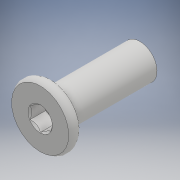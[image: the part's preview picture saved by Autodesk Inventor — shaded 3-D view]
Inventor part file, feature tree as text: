
AUTODESK INVENTOR PART (.ipt)
format: ipt  version: 2018.3 (Build 223284000, 284)  size: 115,712 bytes
history: native  units: mm
features: other x2, extrude x1, sketch x1
ambient origin geometry x8: Origin, YZ Plane, XZ Plane, XY Plane, X Axis, Y Axis, Z Axis, Center Point
bodies: Body1 (feature_tree)
feature tree (4):
  other  "Sólido1"
  extrude  "Extrusión1"  [1 undecoded]
  sketch  "Boceto1"  dims[d0=42.0mm d1=0.0mm]
  other  "Material-C-Beam Linear Actuator 500mm-1"
note: 1 required parameter value undecoded (feature->parameter linkage not recoverable at this tier; creation-order binding heuristic only, values carry confidence <= 0.55)
